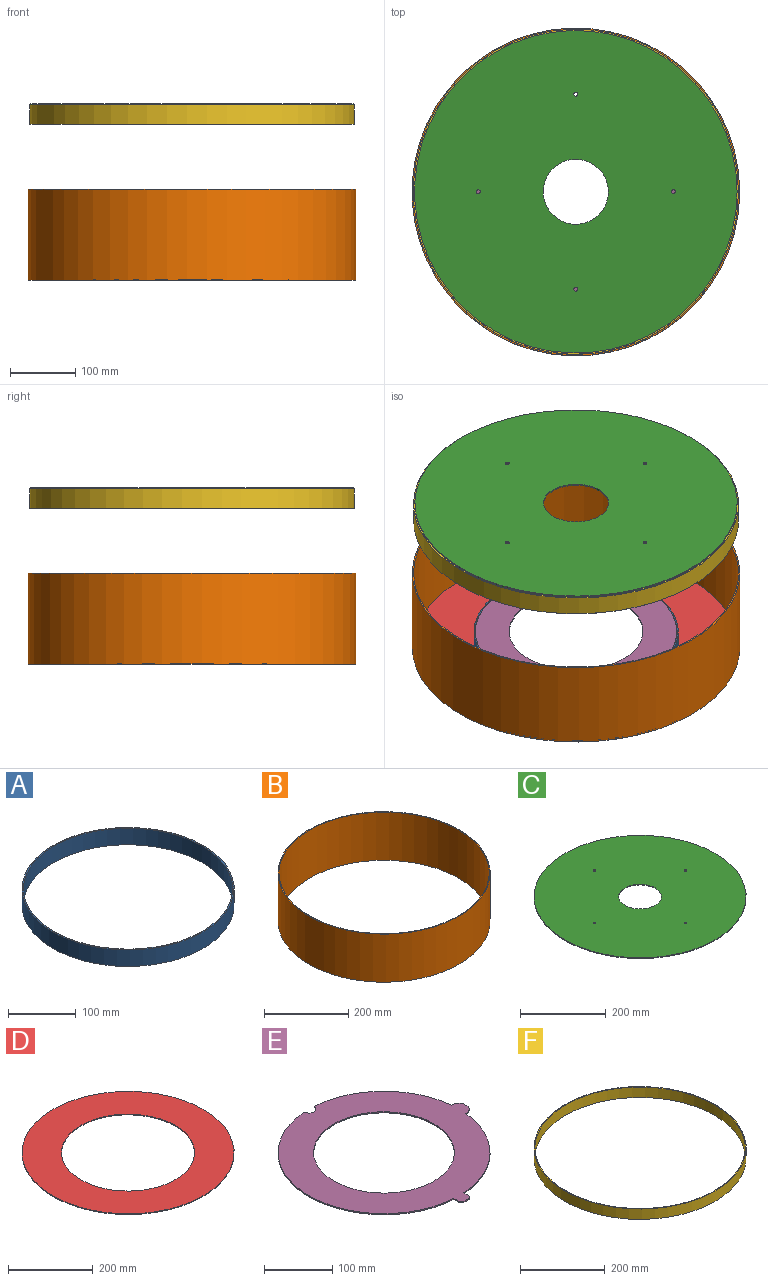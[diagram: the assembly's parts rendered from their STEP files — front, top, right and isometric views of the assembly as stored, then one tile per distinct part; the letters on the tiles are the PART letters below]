
ASSEMBLY  parts=6 mates=5
PART A: 4 faces, bbox 314x314x30 mm
  f0: cylinder r=155mm len=310mm, axis (0,0,-1), area 29216.8mm2, adj f2,f3
  f1: cylinder r=157mm len=314mm, axis (0,0,-1), area 29593.8mm2, adj f2,f3
  f2: plane 314x314mm, normal (0,0,1), area 1960.4mm2, adj f0,f1
  f3: plane 314x314mm, normal (0,0,-1), area 1960.4mm2, adj f0,f1
PART B: 4 faces, bbox 504x504x140 mm
  f0: cylinder r=250mm len=500mm, axis (0,0,-1), area 219911.5mm2, adj f2,f3
  f1: cylinder r=252mm len=504mm, axis (0,0,-1), area 221670.8mm2, adj f2,f3
  f2: plane 504x504mm, normal (0,0,1), area 3154.2mm2, adj f0,f1
  f3: plane 504x504mm, normal (0,0,-1), area 3154.2mm2, adj f0,f1
PART C: 8 faces, bbox 496x496x2 mm
  f0: cylinder r=50mm len=100mm, axis (0,0,-1), area 628.3mm2, adj f6,f7
  f1: cylinder r=3mm len=6mm, axis (0,0,-1), area 37.7mm2, adj f6,f7
  f2: cylinder r=3mm len=6mm, axis (0,0,-1), area 37.7mm2, adj f6,f7
  f3: cylinder r=3mm len=6mm, axis (0,0,-1), area 37.7mm2, adj f6,f7
  f4: cylinder r=3mm len=6mm, axis (0,0,-1), area 37.7mm2, adj f6,f7
  f5: cylinder r=248mm len=496mm, axis (0,0,-1), area 3116.5mm2, adj f6,f7
  f6: plane 496x496mm, normal (0,0,1), area 185253.4mm2, adj f0,f1,f2,f3,f4,f5
  f7: plane 496x496mm, normal (0,0,-1), area 185253.4mm2, adj f0,f1,f2,f3,f4,f5
PART D: 4 faces, bbox 500x500x2 mm
  f0: cylinder r=157mm len=314mm, axis (0,0,-1), area 1972.9mm2, adj f2,f3
  f1: cylinder r=250mm len=500mm, axis (0,0,-1), area 3141.6mm2, adj f2,f3
  f2: plane 500x500mm, normal (0,0,1), area 118912.4mm2, adj f0,f1
  f3: plane 500x500mm, normal (0,0,-1), area 118912.4mm2, adj f0,f1
PART E: 16 faces, bbox 324.3x324.7x2 mm
  f0: plane 9.22x2mm, normal (1,0,0), area 18.4mm2, adj f1,f13,f14,f15
  f1: cylinder r=15mm len=13.55mm, axis (0,0,-1), area 36.3mm2, adj f0,f2,f14,f15
  f2: plane 2x1.45mm, normal (0,1,0), area 2.9mm2, adj f1,f3,f14,f15
  f3: cylinder r=155mm len=144.27mm, axis (0,0,-1), area 436.9mm2, adj f2,f4,f14,f15
  f4: cylinder r=10.01mm len=20mm, axis (0,0,-1), area 61.6mm2, adj f3,f5,f14,f15
  f5: cylinder r=155mm len=309.35mm, axis (0,0,-1), area 933.9mm2, adj f4,f6,f14,f15
  f6: plane 10.32x2mm, normal (-1,0,0), area 20.6mm2, adj f5,f7,f14,f15
  f7: cylinder r=5mm len=5mm, axis (0,0,-1), area 15.7mm2, adj f6,f8,f14,f15
  f8: plane 10x2mm, normal (0,-1,0), area 20mm2, adj f7,f9,f14,f15
  f9: cylinder r=5mm len=5mm, axis (0,0,-1), area 15.7mm2, adj f8,f10,f14,f15
  f10: plane 10.32x2mm, normal (1,0,0), area 20.6mm2, adj f9,f11,f14,f15
  f11: cylinder r=155mm len=144.27mm, axis (0,0,-1), area 436.9mm2, adj f10,f13,f14,f15
  f12: cylinder r=103mm len=206mm, axis (0,0,-1), area 1294.3mm2, adj f14,f15
  f13: cylinder r=15mm len=15mm, axis (0,0,-1), area 39.2mm2, adj f0,f11,f14,f15
  f14: plane 324.68x324.27mm, normal (0,0,1), area 42640.1mm2, adj f0,f1,f2,f3,f4,f5,f6,f7
  f15: plane 324.68x324.27mm, normal (0,0,-1), area 42640.1mm2, adj f0,f1,f2,f3,f4,f5,f6,f7
PART F: 4 faces, bbox 500x500x30 mm
  f0: cylinder r=248mm len=496mm, axis (0,0,-1), area 46746.9mm2, adj f2,f3
  f1: cylinder r=250mm len=500mm, axis (0,0,-1), area 47123.9mm2, adj f2,f3
  f2: plane 500x500mm, normal (0,0,1), area 3129mm2, adj f0,f1
  f3: plane 500x500mm, normal (0,0,-1), area 3129mm2, adj f0,f1
PLACE A t=(-1044.84,30.48,-107.79)mm
PLACE B t=(-2226.86,30.48,-107.79)mm
PLACE C t=(65.88,792.11,162.21)mm
PLACE D t=(-1535.55,30.48,-107.79)mm
PLACE E t=(-495.63,30.48,-79.79)mm
PLACE F t=(65.88,30.48,132.21)mm
MATE fastened F.f1 <-> C.f0  axis (0,0,1) through (65.88,30.48,162.21)mm
MATE fastened A.f0 <-> D.f0  axis (0,0,-1) through (65.88,30.48,-107.79)mm
MATE fastened D.f1 <-> B.f0  axis (0,0,-1) through (65.88,30.48,-107.79)mm
MATE fastened E.f3 <-> A.f0  axis (0,0,1) through (65.88,30.48,-77.79)mm
MATE fastened B.f0 <-> F.f1  axis (0,0,-1) through (65.88,30.48,-37.79)mm
